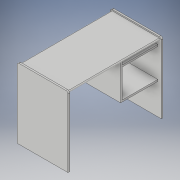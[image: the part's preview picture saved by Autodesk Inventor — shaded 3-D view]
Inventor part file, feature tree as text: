
AUTODESK INVENTOR PART (.ipt)
format: ipt  version: 2017 (Build 210142000, 142)  size: 187,904 bytes
history: native  units: in
note: dims shown in document units (in); Inventor stores cm internally (conversion verified against a paired STEP export)
features: other x3, extrude x1, sketch x1
ambient origin geometry x8: Origin, YZ Plane, XZ Plane, XY Plane, X Axis, Y Axis, Z Axis, Center Point
bodies: Solid1 (feature_tree)
feature tree (5):
  other  "table.ipt"
  extrude  "Extrusion1"  Depth=0.0328in TaperAngle=0.0deg
  other  "Solid1::table.ipt"
  other  "TaggingFeature1"
  sketch  "Sketch1"  dims[d0=0.0328in d1=1.5in d2=0.0in]
